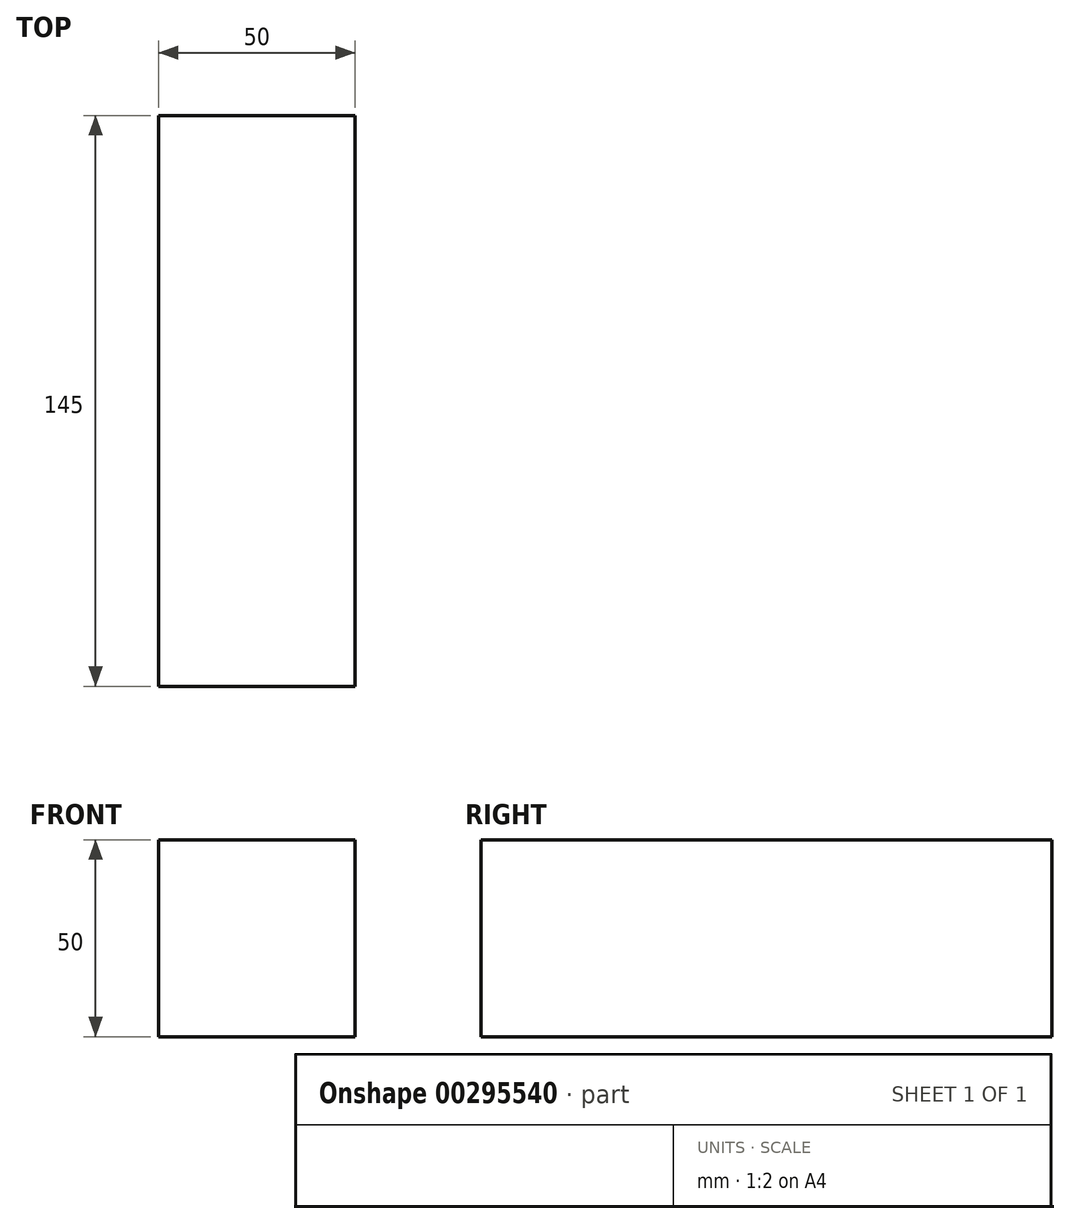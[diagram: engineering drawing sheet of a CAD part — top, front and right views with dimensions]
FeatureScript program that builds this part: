
annotation { "Feature Type Name" : "Feature", "Feature Type Description" : "" }
export const myFeature = defineFeature(function(context is Context, id is Id, definition is map)
    precondition{}
    {
        {
            var Q0;
            Q0=qCreatedBy(makeId("Front.planeOp"),FACE);
            var sketch = newSketch(context, id + "F0", { "sketchPlane" : qUnion([Q0])});
            skLineSegment(sketch, "E0.bottom", {"start": v(-25, 25) * mm, "end": v(25, 25) * mm});
            skLineSegment(sketch, "E0.top", {"start": v(-25, -25) * mm, "end": v(25, -25) * mm});
            skLineSegment(sketch, "E0.left", {"start": v(-25, 25) * mm, "end": v(-25, -25) * mm});
            skLineSegment(sketch, "E0.right", {"start": v(25, 25) * mm, "end": v(25, -25) * mm});
            skLineSegment(sketch, "E1", {"start": v(-25, 25) * mm, "end": v(25, -25) * mm, "construction": true});
            skSolve(sketch);
        }
        {
            var Q0;
            Q0=makeQuery(id+"F0.imprint","IMPRINT",FACE,{"disambiguationData":[TD([[makeQuery(id+"F0.imprint","IMPRINT",EDGE,{"derivedFrom":sQuery(id+"F0.wireOp",EDGE,"E0.bottom")}),-1.0]])]});
            extrude(context, id + "F1", {"entities" : qUnion([Q0]), "oppositeDirection" : true, "depth" : 145 * mm});
        }
    });
